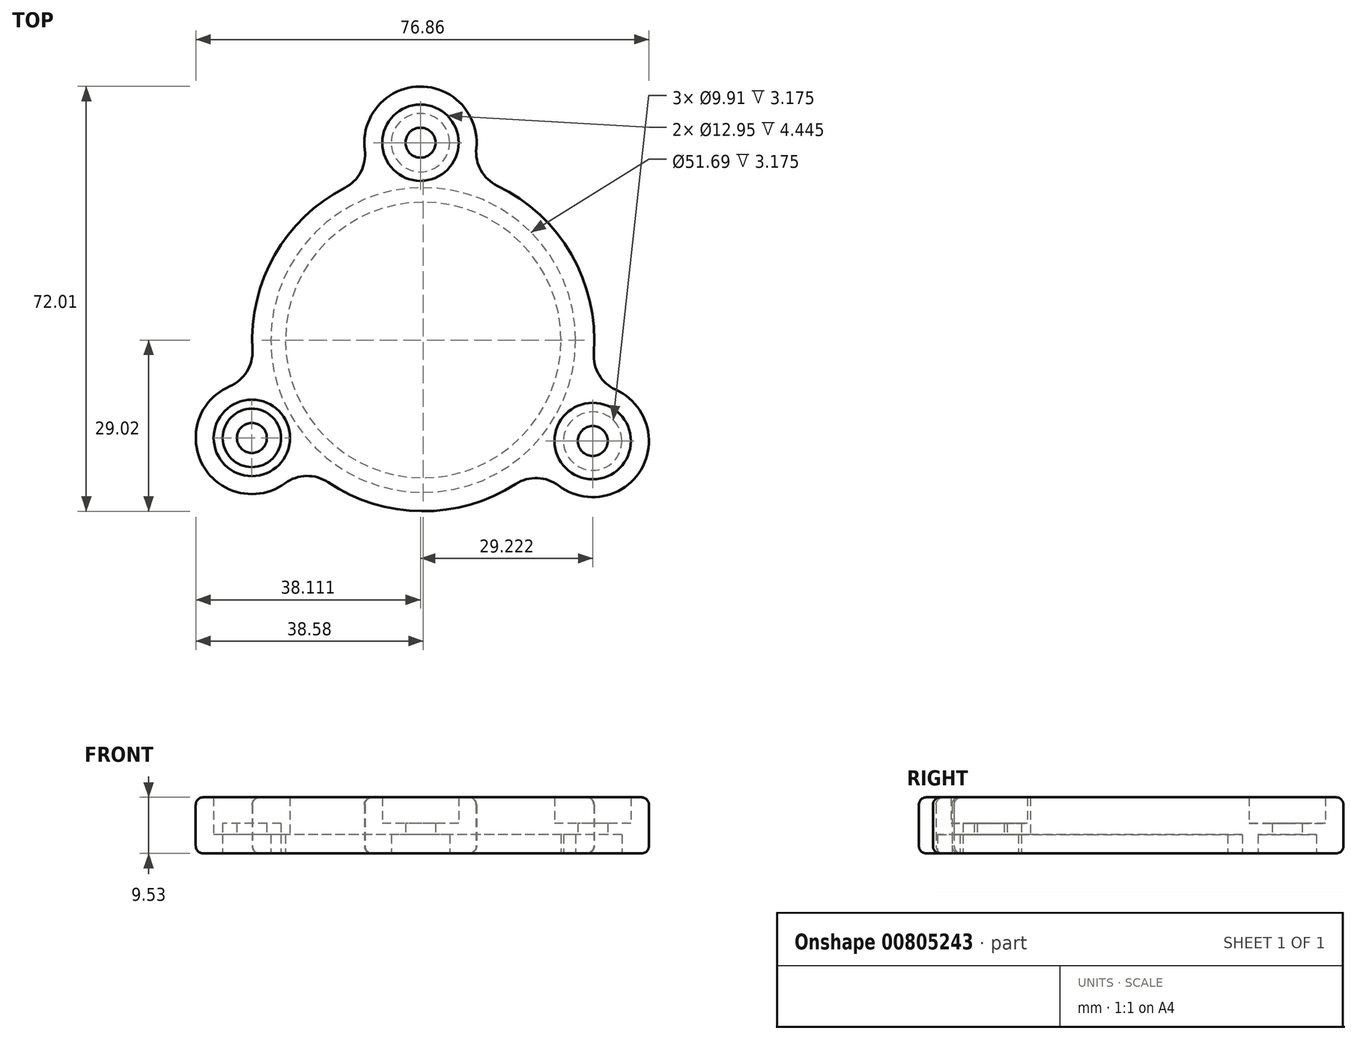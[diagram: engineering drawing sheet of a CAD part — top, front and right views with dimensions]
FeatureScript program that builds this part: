
annotation { "Feature Type Name" : "Feature", "Feature Type Description" : "" }
export const myFeature = defineFeature(function(context is Context, id is Id, definition is map)
    precondition{}
    {
        {
            var Q0;
            Q0=qCreatedBy(makeId("Top.planeOp"),FACE);
            var sketch = newSketch(context, id + "F0", { "sketchPlane" : qUnion([Q0])});
            skCircle(sketch, "E0", {"center": v(0, 0) * mm, "radius": 25.84 * mm});
            skCircle(sketch, "E1", {"center": v(0, 0) * mm, "radius": 23.37 * mm});
            skLineSegment(sketch, "E2", {"start": v(-57, -31.6) * mm, "end": v(-37.45, -21.1) * mm});
            skLineSegment(sketch, "E3", {"start": v(0, 48.63) * mm, "end": v(-0.32, 38.41) * mm});
            skCircle(sketch, "E4", {"center": v(-0.47, 33.46) * mm, "radius": 4.95 * mm});
            skCircle(sketch, "E5", {"center": v(28.75, -17.12) * mm, "radius": 4.95 * mm});
            skArc(sketch, "E6", {"start": v(-32.81, -7.84) * mm, "mid": v(-37.33, -21.32) * mm, "end": v(-23.43, -24.28) * mm});
            skCircle(sketch, "E7", {"center": v(-29.06, -16.6) * mm, "radius": 4.95 * mm});
            skArc(sketch, "E8", {"start": v(9, 32.51) * mm, "mid": v(-0.6, 42.99) * mm, "end": v(-9.92, 32.25) * mm});
            skArc(sketch, "E9", {"start": v(22.98, -24.7) * mm, "mid": v(36.94, -22) * mm, "end": v(32.66, -8.43) * mm});
            skLineSegment(sketch, "E10.trimOffspring", {"start": v(37, -21.88) * mm, "end": v(57.71, -34.7) * mm});
            skPoint(sketch, "E11.visualSharp", {"position": v(32.39, -8.32) * mm});
            skPoint(sketch, "E12.visualSharp", {"position": v(22.95, -24.67) * mm});
            skPoint(sketch, "E13.visualSharp", {"position": v(8.97, 32.2) * mm});
            skPoint(sketch, "E14.visualSharp", {"position": v(-9.91, 32.2) * mm});
            skPoint(sketch, "E15.visualSharp", {"position": v(-32.7, -7.8) * mm});
            skPoint(sketch, "E16.visualSharp", {"position": v(-23.25, -24.14) * mm});
            skArc(sketch, "E17", {"start": v(-13.3, 25.8) * mm, "mid": v(-25.2, 14.4) * mm, "end": v(-28.97, -1.64) * mm});
            skArc(sketch, "E18.trimOffspring", {"start": v(28.94, -2.17) * mm, "mid": v(25.13, 14.52) * mm, "end": v(12.58, 26.15) * mm});
            skArc(sketch, "E19.trimOffspring", {"start": v(-16.14, -24.12) * mm, "mid": v(-0.26, -29.02) * mm, "end": v(15.7, -24.4) * mm});
            skPoint(sketch, "E20.visualSharp", {"position": v(-8.16, 27.85) * mm});
            skArc(sketch, "E20.filletArc", {"start": v(-13.3, 25.8) * mm, "mid": v(-10.6, 28.48) * mm, "end": v(-9.92, 32.25) * mm});
            skPoint(sketch, "E21.visualSharp", {"position": v(7.38, 28.07) * mm});
            skArc(sketch, "E21.filletArc", {"start": v(9, 32.51) * mm, "mid": v(9.79, 28.77) * mm, "end": v(12.58, 26.15) * mm});
            skPoint(sketch, "E22.visualSharp", {"position": v(28, -7.63) * mm});
            skArc(sketch, "E22.filletArc", {"start": v(28.94, -2.17) * mm, "mid": v(29.81, -5.9) * mm, "end": v(32.66, -8.43) * mm});
            skPoint(sketch, "E23.visualSharp", {"position": v(20.05, -20.98) * mm});
            skArc(sketch, "E23.filletArc", {"start": v(22.98, -24.7) * mm, "mid": v(19.39, -23.4) * mm, "end": v(15.7, -24.4) * mm});
            skPoint(sketch, "E24.visualSharp", {"position": v(-20.42, -20.61) * mm});
            skArc(sketch, "E24.filletArc", {"start": v(-16.14, -24.12) * mm, "mid": v(-19.8, -23.05) * mm, "end": v(-23.43, -24.28) * mm});
            skPoint(sketch, "E25.visualSharp", {"position": v(-28.13, -7.12) * mm});
            skArc(sketch, "E25.filletArc", {"start": v(-32.81, -7.84) * mm, "mid": v(-29.91, -5.35) * mm, "end": v(-28.97, -1.64) * mm});
            skSolve(sketch);
        }
        {
            var Q0;
            Q0=makeQuery(id+"F0.imprint","IMPRINT",FACE,{"disambiguationData":[TD([[makeQuery(id+"F0.imprint","IMPRINT",EDGE,{"derivedFrom":sQuery(id+"F0.wireOp",EDGE,"E0")}),-1.0]])]});
            var Q1;
            Q1=makeQuery(id+"F0.imprint","IMPRINT",FACE,{"disambiguationData":[TD([[makeQuery(id+"F0.imprint","IMPRINT",EDGE,{"derivedFrom":sQuery(id+"F0.wireOp",EDGE,"E1")}),1.0]])]});
            extrude(context, id + "F1", {"entities" : qUnion([Q0, Q1]), "depth" : 3.17 * mm, "offsetDistance" : 25.4 * mm});
        }
        {
            var Q0;
            Q0=makeQuery(id+"F1.opExtrude","CAP_FACE",FACE,{"disambiguationData":[OSD([sQuery(id+"F0.wireOp",EDGE,"E0"),sQuery(id+"F0.wireOp",EDGE,"E4"),sQuery(id+"F0.wireOp",EDGE,"E5"),sQuery(id+"F0.wireOp",EDGE,"E6"),sQuery(id+"F0.wireOp",EDGE,"E7"),sQuery(id+"F0.wireOp",EDGE,"E8"),sQuery(id+"F0.wireOp",EDGE,"E9"),sQuery(id+"F0.wireOp",EDGE,"E17"),sQuery(id+"F0.wireOp",EDGE,"E18.trimOffspring"),sQuery(id+"F0.wireOp",EDGE,"E19.trimOffspring"),sQuery(id+"F0.wireOp",EDGE,"E20.filletArc"),sQuery(id+"F0.wireOp",EDGE,"E21.filletArc"),sQuery(id+"F0.wireOp",EDGE,"E22.filletArc"),sQuery(id+"F0.wireOp",EDGE,"E23.filletArc"),sQuery(id+"F0.wireOp",EDGE,"E24.filletArc"),sQuery(id+"F0.wireOp",EDGE,"E25.filletArc")])],"isStart":false});
            var sketch = newSketch(context, id + "F2", { "sketchPlane" : qUnion([Q0])});
            skArc(sketch, "E26.0.0", {"start": v(22.98, -24.7) * mm, "mid": v(36.94, -22) * mm, "end": v(32.66, -8.43) * mm});
            skArc(sketch, "E26.0.1", {"start": v(32.66, -8.43) * mm, "mid": v(29.81, -5.9) * mm, "end": v(28.94, -2.17) * mm});
            skArc(sketch, "E26.0.2", {"start": v(28.94, -2.17) * mm, "mid": v(25.13, 14.52) * mm, "end": v(12.58, 26.15) * mm});
            skArc(sketch, "E26.0.3", {"start": v(12.58, 26.15) * mm, "mid": v(9.79, 28.77) * mm, "end": v(9, 32.51) * mm});
            skArc(sketch, "E26.0.4", {"start": v(9, 32.51) * mm, "mid": v(-0.6, 42.99) * mm, "end": v(-9.92, 32.25) * mm});
            skArc(sketch, "E26.0.5", {"start": v(-9.92, 32.25) * mm, "mid": v(-10.6, 28.48) * mm, "end": v(-13.3, 25.8) * mm});
            skArc(sketch, "E26.0.6", {"start": v(-13.3, 25.8) * mm, "mid": v(-25.2, 14.4) * mm, "end": v(-28.97, -1.64) * mm});
            skArc(sketch, "E26.0.7", {"start": v(-28.97, -1.64) * mm, "mid": v(-29.91, -5.35) * mm, "end": v(-32.81, -7.84) * mm});
            skArc(sketch, "E26.0.8", {"start": v(-32.81, -7.84) * mm, "mid": v(-37.33, -21.32) * mm, "end": v(-23.43, -24.28) * mm});
            skArc(sketch, "E26.0.9", {"start": v(-23.43, -24.28) * mm, "mid": v(-19.8, -23.05) * mm, "end": v(-16.14, -24.12) * mm});
            skArc(sketch, "E26.0.10", {"start": v(-16.14, -24.12) * mm, "mid": v(-0.26, -29.02) * mm, "end": v(15.7, -24.4) * mm});
            skArc(sketch, "E26.0.11", {"start": v(15.7, -24.4) * mm, "mid": v(19.39, -23.4) * mm, "end": v(22.98, -24.7) * mm});
            skCircle(sketch, "E27.0.0", {"center": v(0, 0) * mm, "radius": 23.37 * mm});
            skCircle(sketch, "E28", {"center": v(-0.47, 33.46) * mm, "radius": 6.48 * mm});
            skCircle(sketch, "E29", {"center": v(-29.06, -16.6) * mm, "radius": 6.48 * mm});
            skCircle(sketch, "E30", {"center": v(28.75, -17.12) * mm, "radius": 6.48 * mm});
            skSolve(sketch);
        }
        {
            var Q0;
            Q0=makeQuery(id+"F2.imprint","IMPRINT",FACE,{"disambiguationData":[TD([[makeQuery(id+"F2.imprint","IMPRINT",EDGE,{"derivedFrom":sQuery(id+"F2.wireOp",EDGE,"E26.0.0")}),1.0]])]});
            var Q1;
            Q1=makeQuery(id+"F2.imprint","IMPRINT",FACE,{"disambiguationData":[TD([[makeQuery(id+"F2.imprint","IMPRINT",EDGE,{"derivedFrom":sQuery(id+"F2.wireOp",EDGE,"E27.0.0")}),-1.0]])]});
            var Q2;
            Q2=makeQuery(id+"F2.imprint","IMPRINT",FACE,{"disambiguationData":[TD([[makeQuery(id+"F2.imprint","IMPRINT",EDGE,{"derivedFrom":sQuery(id+"F2.wireOp",EDGE,"E27.0.0")}),1.0]])]});
            extrude(context, id + "F3", {"entities" : qUnion([Q0, Q1, Q2]), "operationType" : NewBodyOperationType.ADD, "depth" : 6.35 * mm, "offsetDistance" : 25.4 * mm});
        }
        {
            var Q0;
            Q0=makeQuery(id+"F1.opExtrude","CAP_EDGE",EDGE,{"disambiguationData":[OSD([sQuery(id+"F0.wireOp",EDGE,"E8")])],"isStart":true});
            var Q1;
            Q1=makeQuery(id+"F3.opExtrude","CAP_EDGE",EDGE,{"disambiguationData":[OSD([sQuery(id+"F2.wireOp",EDGE,"E26.0.9")])],"isStart":false});
            fillet(context, id + "F4", {"entities" : qUnion([Q0, Q1]), "radius" : 1.27 * mm, "tangentPropagation" : true, "allowEdgeOverflow" : false});
        }
        {
            var Q0;
            {var subQ0=sQuery(id+"F0.wireOp",EDGE,"E7");Q0=makeQuery(id+"F3.boolean.opBoolean","SPLIT",FACE,{"disambiguationData":[TD([makeQuery(id+"F1.opExtrude","SWEPT_FACE",FACE,{"disambiguationData":[OSD([subQ0])]})])],"derivedFrom":makeQuery(id+"F1.opExtrude","CAP_FACE",FACE,{"disambiguationData":[OSD([sQuery(id+"F0.wireOp",EDGE,"E0"),sQuery(id+"F0.wireOp",EDGE,"E4"),sQuery(id+"F0.wireOp",EDGE,"E5"),sQuery(id+"F0.wireOp",EDGE,"E6"),subQ0,sQuery(id+"F0.wireOp",EDGE,"E8"),sQuery(id+"F0.wireOp",EDGE,"E9"),sQuery(id+"F0.wireOp",EDGE,"E17"),sQuery(id+"F0.wireOp",EDGE,"E18.trimOffspring"),sQuery(id+"F0.wireOp",EDGE,"E19.trimOffspring"),sQuery(id+"F0.wireOp",EDGE,"E20.filletArc"),sQuery(id+"F0.wireOp",EDGE,"E21.filletArc"),sQuery(id+"F0.wireOp",EDGE,"E22.filletArc"),sQuery(id+"F0.wireOp",EDGE,"E23.filletArc"),sQuery(id+"F0.wireOp",EDGE,"E24.filletArc"),sQuery(id+"F0.wireOp",EDGE,"E25.filletArc")])],"isStart":false})});}
            var sketch = newSketch(context, id + "F5", { "sketchPlane" : qUnion([Q0])});
            skCircle(sketch, "E31.0", {"center": v(-29.06, -16.6) * mm, "radius": 6.48 * mm});
            skCircle(sketch, "E32.0", {"center": v(28.75, -17.12) * mm, "radius": 6.48 * mm});
            skCircle(sketch, "E33.0", {"center": v(-0.47, 33.46) * mm, "radius": 6.48 * mm});
            skCircle(sketch, "E34", {"center": v(-29.06, -16.6) * mm, "radius": 2.54 * mm});
            skCircle(sketch, "E35", {"center": v(28.75, -17.12) * mm, "radius": 2.54 * mm});
            skCircle(sketch, "E36", {"center": v(-0.47, 33.46) * mm, "radius": 2.54 * mm});
            skSolve(sketch);
        }
        {
            var Q0;
            Q0=makeQuery(id+"F5.imprint","IMPRINT",FACE,{"disambiguationData":[TD([[makeQuery(id+"F5.imprint","IMPRINT",EDGE,{"derivedFrom":sQuery(id+"F5.wireOp",EDGE,"E33.0")}),1.0]])]});
            var Q1;
            Q1=makeQuery(id+"F5.imprint","IMPRINT",FACE,{"disambiguationData":[TD([[makeQuery(id+"F5.imprint","IMPRINT",EDGE,{"derivedFrom":sQuery(id+"F5.wireOp",EDGE,"E31.0")}),1.0]])]});
            var Q2;
            Q2=makeQuery(id+"F5.imprint","IMPRINT",FACE,{"disambiguationData":[TD([[makeQuery(id+"F5.imprint","IMPRINT",EDGE,{"derivedFrom":sQuery(id+"F5.wireOp",EDGE,"E34")}),-1.0]])]});
            var Q3;
            Q3=makeQuery(id+"F5.imprint","IMPRINT",FACE,{"disambiguationData":[TD([[makeQuery(id+"F5.imprint","IMPRINT",EDGE,{"derivedFrom":sQuery(id+"F5.wireOp",EDGE,"E32.0")}),1.0]])]});
            extrude(context, id + "F6", {"entities" : qUnion([Q0, Q1, Q2, Q3]), "operationType" : NewBodyOperationType.ADD, "depth" : 1.9 * mm, "offsetDistance" : 25.4 * mm});
        }
    });
